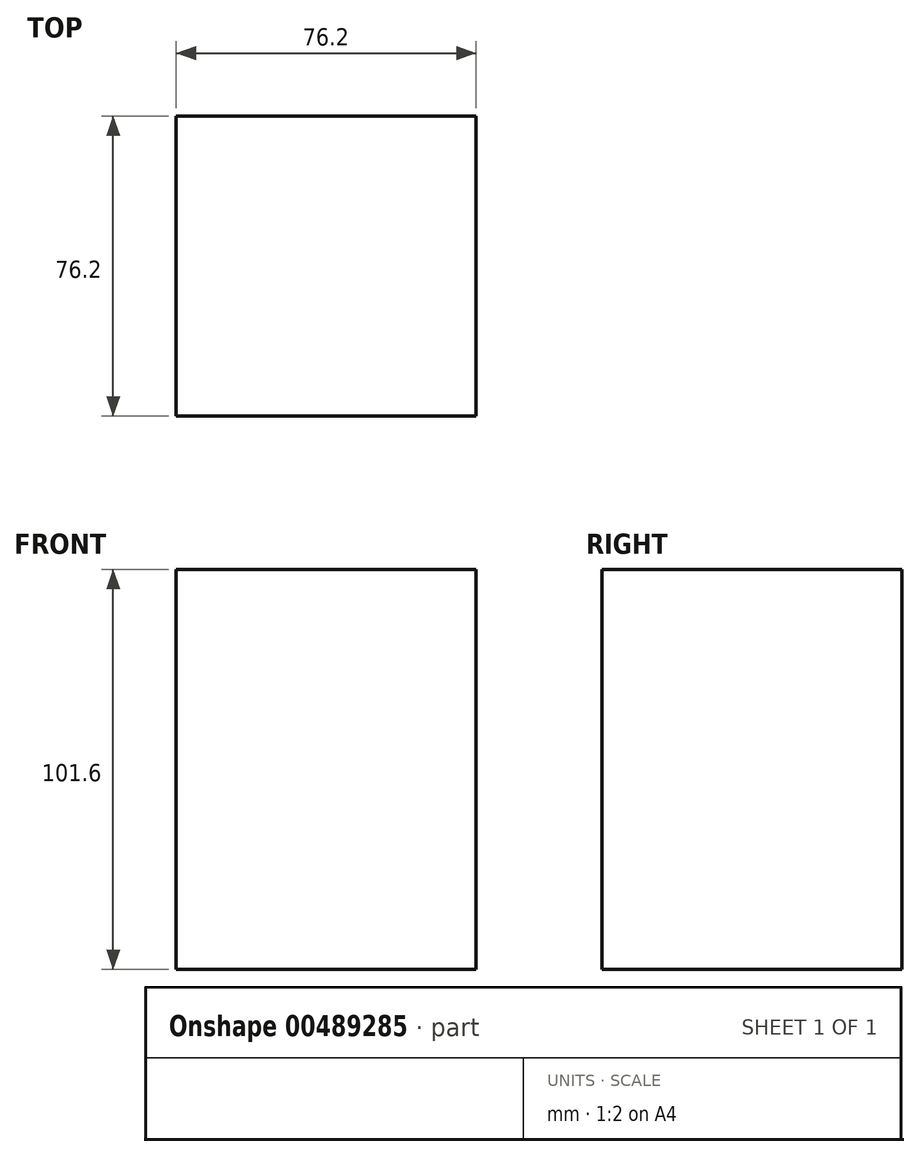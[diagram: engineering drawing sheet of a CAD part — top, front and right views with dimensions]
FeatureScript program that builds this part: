
annotation { "Feature Type Name" : "Feature", "Feature Type Description" : "" }
export const myFeature = defineFeature(function(context is Context, id is Id, definition is map)
    precondition{}
    {
        {
            var Q0;
            Q0=qCreatedBy(makeId("Front.planeOp"),FACE);
            var sketch = newSketch(context, id + "F0", { "sketchPlane" : qUnion([Q0])});
            skLineSegment(sketch, "E0.bottom", {"start": v(38.1, 71.63) * mm, "end": v(-38.1, 71.63) * mm});
            skLineSegment(sketch, "E0.top", {"start": v(38.1, -29.97) * mm, "end": v(-38.1, -29.97) * mm});
            skLineSegment(sketch, "E0.left", {"start": v(38.1, 71.63) * mm, "end": v(38.1, -29.97) * mm});
            skLineSegment(sketch, "E0.right", {"start": v(-38.1, 71.63) * mm, "end": v(-38.1, -29.97) * mm});
            skPoint(sketch, "E0.middle", {"position": v(0, 20.83) * mm});
            skSolve(sketch);
        }
        {
            var Q0;
            Q0 = qSketchRegion(id + "F0", true);
            extrude(context, id + "F1", {"entities" : qUnion([Q0]), "endBound" : BoundingType.SYMMETRIC, "depth" : 76.2 * mm});
        }
        {
            var Q0;
            Q0=makeQuery(id+"F1.opExtrude","SWEPT_FACE",FACE,{"disambiguationData":[OSD([sQuery(id+"F0.wireOp",EDGE,"E0.bottom")])]});
            var sketch = newSketch(context, id + "F2", { "sketchPlane" : qUnion([Q0])});
            skCircle(sketch, "E1", {"center": v(0, 0) * mm, "radius": 17.13 * mm});
            skSolve(sketch);
        }
        {
            var Q0;
            Q0=sQuery(id+"F2.wireOp",EDGE,"E1");
            var Q1;
            Q1=makeQuery(id+"F1.opExtrude","CAP_EDGE",EDGE,{"disambiguationData":[OSD([sQuery(id+"F0.wireOp",EDGE,"E0.bottom")])],"isStart":true});
            revolve(context, id + "F3", {"bodyType" : ToolBodyType.SURFACE, "surfaceEntities" : qUnion([Q0]), "axis" : qUnion([Q1]), "revolveType" : RevolveType.FULL});
        }
    });
